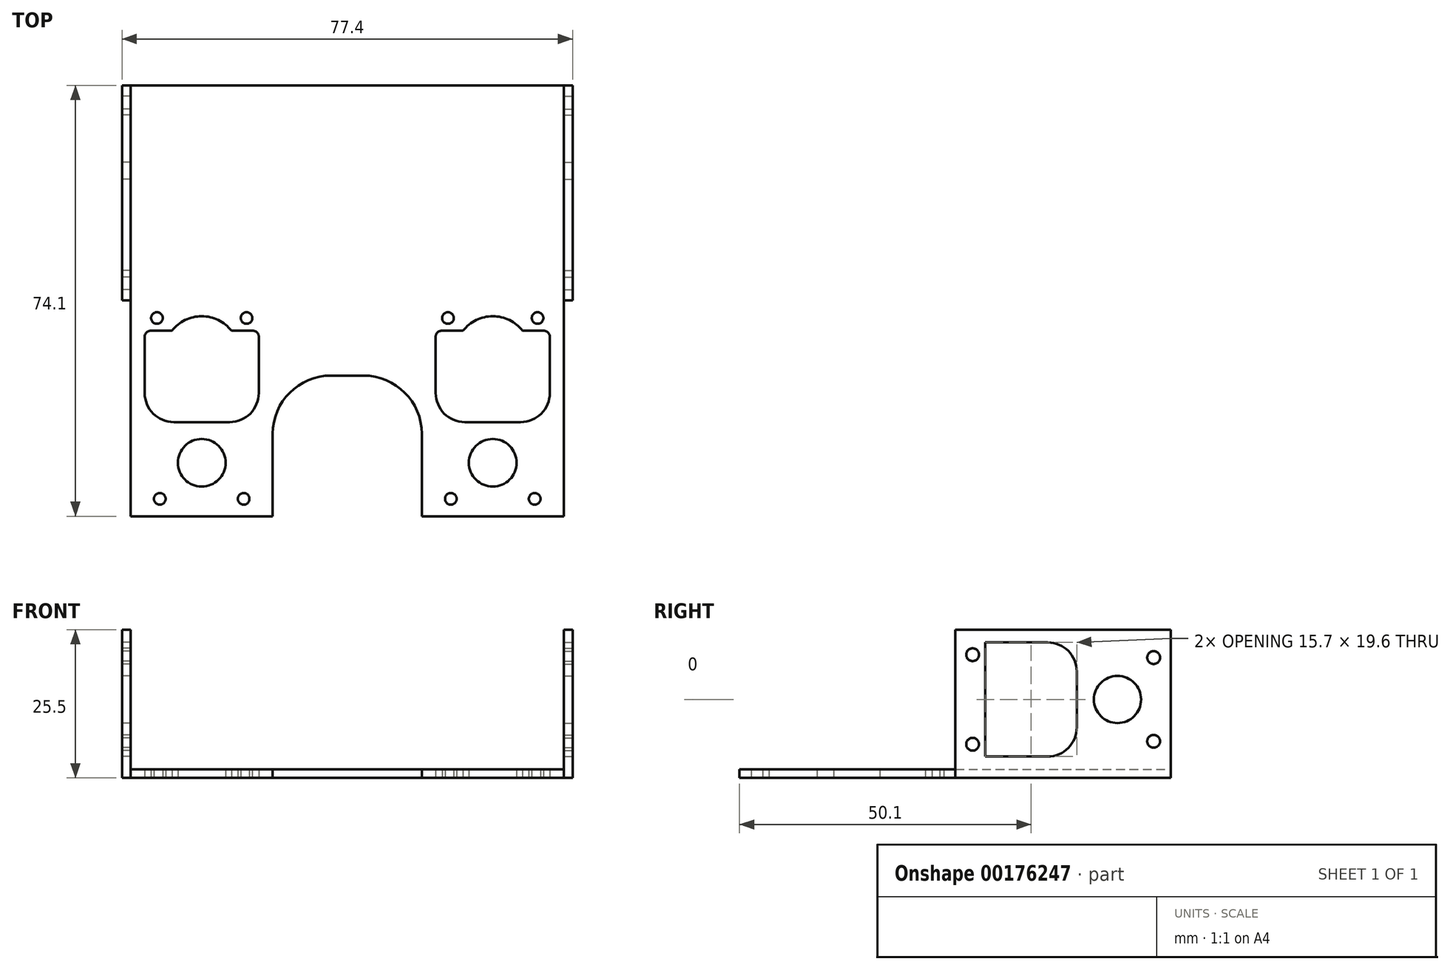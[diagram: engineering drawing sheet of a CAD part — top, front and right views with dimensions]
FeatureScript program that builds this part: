
annotation { "Feature Type Name" : "Feature", "Feature Type Description" : "" }
export const myFeature = defineFeature(function(context is Context, id is Id, definition is map)
    precondition{}
    {
        {
            var Q0;
            Q0=qCreatedBy(makeId("Top.planeOp"),FACE);
            var sketch = newSketch(context, id + "F0", { "sketchPlane" : qUnion([Q0])});
            skLineSegment(sketch, "E0.bottom", {"start": v(37.2, -19.55) * mm, "end": v(-37.2, -19.55) * mm});
            skLineSegment(sketch, "E0.top", {"start": v(37.2, 19.55) * mm, "end": v(-37.2, 19.55) * mm});
            skLineSegment(sketch, "E0.left", {"start": v(37.2, -19.55) * mm, "end": v(37.2, 19.55) * mm});
            skLineSegment(sketch, "E0.right", {"start": v(-37.2, -19.55) * mm, "end": v(-37.2, 19.55) * mm});
            skPoint(sketch, "E0.middle", {"position": v(0, 0) * mm});
            skCircle(sketch, "E1", {"center": v(25, 8.35) * mm, "radius": 4.1 * mm, "construction": true});
            skCircle(sketch, "E2", {"center": v(32.2, 14.55) * mm, "radius": 1 * mm, "construction": true});
            skLineSegment(sketch, "E3.bottom", {"start": v(33.8, -14.35) * mm, "end": v(30.12, -14.35) * mm, "construction": true});
            skLineSegment(sketch, "E3.top", {"start": v(29.8, 1.35) * mm, "end": v(20.2, 1.35) * mm, "construction": true});
            skLineSegment(sketch, "E3.left", {"start": v(34.8, -13.35) * mm, "end": v(34.8, -3.65) * mm, "construction": true});
            skLineSegment(sketch, "E3.right", {"start": v(15.2, -13.35) * mm, "end": v(15.2, -3.65) * mm, "construction": true});
            skPoint(sketch, "E3.middle", {"position": v(25, -6.5) * mm});
            skCircle(sketch, "E4", {"center": v(32.2, -16.55) * mm, "radius": 1 * mm});
            skPoint(sketch, "E5.visualSharp", {"position": v(15.2, 1.35) * mm});
            skArc(sketch, "E5.filletArc", {"start": v(20.2, 1.35) * mm, "mid": v(16.66, -0.11) * mm, "end": v(15.2, -3.65) * mm, "construction": true});
            skPoint(sketch, "E6.visualSharp", {"position": v(34.8, 1.35) * mm});
            skArc(sketch, "E6.filletArc", {"start": v(34.8, -3.65) * mm, "mid": v(33.34, -0.11) * mm, "end": v(29.8, 1.35) * mm, "construction": true});
            skPoint(sketch, "E7.visualSharp", {"position": v(15.2, -14.35) * mm});
            skArc(sketch, "E7.filletArc", {"start": v(15.2, -13.35) * mm, "mid": v(15.5, -14.06) * mm, "end": v(16.2, -14.35) * mm, "construction": true});
            skPoint(sketch, "E8.visualSharp", {"position": v(34.8, -14.35) * mm});
            skArc(sketch, "E8.filletArc", {"start": v(33.8, -14.35) * mm, "mid": v(34.5, -14.06) * mm, "end": v(34.8, -13.35) * mm, "construction": true});
            skArc(sketch, "E9", {"start": v(19.88, -14.35) * mm, "mid": v(25, -16.85) * mm, "end": v(30.12, -14.35) * mm, "construction": true});
            skLineSegment(sketch, "E10.trimOffspring", {"start": v(19.88, -14.35) * mm, "end": v(16.2, -14.35) * mm, "construction": true});
            skLineSegment(sketch, "E11", {"start": v(25, 19.55) * mm, "end": v(25, -19.55) * mm, "construction": true});
            skCircle(sketch, "E12.MirrorC", {"center": v(17.8, 14.55) * mm, "radius": 1 * mm, "construction": true});
            skCircle(sketch, "E13.MirrorC", {"center": v(17.8, -16.55) * mm, "radius": 1 * mm});
            skLineSegment(sketch, "E14", {"start": v(32.2, 14.55) * mm, "end": v(32.2, -16.55) * mm, "construction": true});
            skLineSegment(sketch, "E15", {"start": v(32.2, -1) * mm, "end": v(0, -1) * mm, "construction": true});
            skArc(sketch, "E16.MirrorCS", {"start": v(15.2, 11.35) * mm, "mid": v(15.5, 12.06) * mm, "end": v(16.2, 12.35) * mm});
            skArc(sketch, "E17.MirrorCS", {"start": v(33.8, 12.35) * mm, "mid": v(34.5, 12.06) * mm, "end": v(34.8, 11.35) * mm});
            skLineSegment(sketch, "E18.MirrorCS", {"start": v(15.2, 11.35) * mm, "end": v(15.2, 1.65) * mm});
            skLineSegment(sketch, "E19.MirrorCS", {"start": v(34.8, 11.35) * mm, "end": v(34.8, 1.65) * mm});
            skPoint(sketch, "E20.MirrorP", {"position": v(34.8, -3.35) * mm});
            skArc(sketch, "E21.MirrorCS", {"start": v(19.88, 12.35) * mm, "mid": v(25, 14.85) * mm, "end": v(30.12, 12.35) * mm});
            skPoint(sketch, "E22.MirrorP", {"position": v(15.2, -3.35) * mm});
            skPoint(sketch, "E23.MirrorP", {"position": v(25, 4.5) * mm});
            skCircle(sketch, "E24.MirrorC", {"center": v(25, -10.35) * mm, "radius": 4.1 * mm});
            skArc(sketch, "E25.MirrorCS", {"start": v(20.2, -3.35) * mm, "mid": v(16.66, -1.89) * mm, "end": v(15.2, 1.65) * mm});
            skLineSegment(sketch, "E26.MirrorCS", {"start": v(19.88, 12.35) * mm, "end": v(16.2, 12.35) * mm});
            skArc(sketch, "E27.MirrorCS", {"start": v(34.8, 1.65) * mm, "mid": v(33.34, -1.89) * mm, "end": v(29.8, -3.35) * mm});
            skPoint(sketch, "E28.MirrorP", {"position": v(34.8, 12.35) * mm});
            skLineSegment(sketch, "E29.MirrorCS", {"start": v(29.8, -3.35) * mm, "end": v(20.2, -3.35) * mm});
            skLineSegment(sketch, "E30.MirrorCS", {"start": v(33.8, 12.35) * mm, "end": v(30.12, 12.35) * mm});
            skPoint(sketch, "E31.MirrorP", {"position": v(15.2, 12.35) * mm});
            skArc(sketch, "E32.MirrorCS", {"start": v(-15.2, -13.35) * mm, "mid": v(-15.5, -14.06) * mm, "end": v(-16.2, -14.35) * mm, "construction": true});
            skArc(sketch, "E33.MirrorCS", {"start": v(-33.8, -14.35) * mm, "mid": v(-34.5, -14.06) * mm, "end": v(-34.8, -13.35) * mm, "construction": true});
            skArc(sketch, "E34.MirrorCS", {"start": v(-33.8, 12.35) * mm, "mid": v(-34.5, 12.06) * mm, "end": v(-34.8, 11.35) * mm});
            skArc(sketch, "E35.MirrorCS", {"start": v(-15.2, 11.35) * mm, "mid": v(-15.5, 12.06) * mm, "end": v(-16.2, 12.35) * mm});
            skPoint(sketch, "E36.MirrorP", {"position": v(-34.8, -14.35) * mm});
            skCircle(sketch, "E37.MirrorC", {"center": v(-25, 8.35) * mm, "radius": 4.1 * mm, "construction": true});
            skLineSegment(sketch, "E38.MirrorCS", {"start": v(-15.2, 11.35) * mm, "end": v(-15.2, 1.65) * mm});
            skArc(sketch, "E39.MirrorCS", {"start": v(-19.88, -14.35) * mm, "mid": v(-25, -16.85) * mm, "end": v(-30.12, -14.35) * mm, "construction": true});
            skCircle(sketch, "E40.MirrorC", {"center": v(-32.2, -16.55) * mm, "radius": 1 * mm});
            skLineSegment(sketch, "E41.MirrorCS", {"start": v(-33.8, -14.35) * mm, "end": v(-30.12, -14.35) * mm, "construction": true});
            skLineSegment(sketch, "E42.MirrorCS", {"start": v(-34.8, -13.35) * mm, "end": v(-34.8, -3.65) * mm, "construction": true});
            skCircle(sketch, "E43.MirrorC", {"center": v(-17.8, -16.55) * mm, "radius": 1 * mm});
            skPoint(sketch, "E44.MirrorP", {"position": v(-25, -6.5) * mm});
            skLineSegment(sketch, "E45.MirrorCS", {"start": v(-15.2, -13.35) * mm, "end": v(-15.2, -3.65) * mm, "construction": true});
            skPoint(sketch, "E46.MirrorP", {"position": v(-34.8, 12.35) * mm});
            skLineSegment(sketch, "E47.MirrorCS", {"start": v(-32.2, 14.55) * mm, "end": v(-32.2, -16.55) * mm, "construction": true});
            skLineSegment(sketch, "E48.MirrorCS", {"start": v(-34.8, 11.35) * mm, "end": v(-34.8, 1.65) * mm});
            skLineSegment(sketch, "E49.MirrorCS", {"start": v(-33.8, 12.35) * mm, "end": v(-30.12, 12.35) * mm});
            skArc(sketch, "E50.MirrorCS", {"start": v(-20.2, -3.35) * mm, "mid": v(-16.66, -1.89) * mm, "end": v(-15.2, 1.65) * mm});
            skArc(sketch, "E51.MirrorCS", {"start": v(-19.88, 12.35) * mm, "mid": v(-25, 14.85) * mm, "end": v(-30.12, 12.35) * mm});
            skLineSegment(sketch, "E52.MirrorCS", {"start": v(-19.88, 12.35) * mm, "end": v(-16.2, 12.35) * mm});
            skArc(sketch, "E53.MirrorCS", {"start": v(-34.8, -3.65) * mm, "mid": v(-33.34, -0.11) * mm, "end": v(-29.8, 1.35) * mm, "construction": true});
            skPoint(sketch, "E54.MirrorP", {"position": v(-15.2, 1.35) * mm});
            skCircle(sketch, "E55.MirrorC", {"center": v(-32.2, 14.55) * mm, "radius": 1 * mm, "construction": true});
            skPoint(sketch, "E56.MirrorP", {"position": v(-34.8, 1.35) * mm});
            skPoint(sketch, "E57.MirrorP", {"position": v(-15.2, -3.35) * mm});
            skLineSegment(sketch, "E58.MirrorCS", {"start": v(-29.8, 1.35) * mm, "end": v(-20.2, 1.35) * mm, "construction": true});
            skLineSegment(sketch, "E59.MirrorCS", {"start": v(-29.8, -3.35) * mm, "end": v(-20.2, -3.35) * mm});
            skPoint(sketch, "E60.MirrorP", {"position": v(-34.8, -3.35) * mm});
            skArc(sketch, "E61.MirrorCS", {"start": v(-20.2, 1.35) * mm, "mid": v(-16.66, -0.11) * mm, "end": v(-15.2, -3.65) * mm, "construction": true});
            skCircle(sketch, "E62.MirrorC", {"center": v(-25, -10.35) * mm, "radius": 4.1 * mm});
            skPoint(sketch, "E63.MirrorP", {"position": v(-15.2, -14.35) * mm});
            skPoint(sketch, "E64.MirrorP", {"position": v(-15.2, 12.35) * mm});
            skPoint(sketch, "E65.MirrorP", {"position": v(-25, 4.5) * mm});
            skArc(sketch, "E66.MirrorCS", {"start": v(-34.8, 1.65) * mm, "mid": v(-33.34, -1.89) * mm, "end": v(-29.8, -3.35) * mm});
            skCircle(sketch, "E67.MirrorC", {"center": v(-17.8, 14.55) * mm, "radius": 1 * mm, "construction": true});
            skLineSegment(sketch, "E68.MirrorCS", {"start": v(-19.88, -14.35) * mm, "end": v(-16.2, -14.35) * mm, "construction": true});
            skCircle(sketch, "E69", {"center": v(32.7, 14.55) * mm, "radius": 1 * mm, "construction": true});
            skCircle(sketch, "E70.MirrorC", {"center": v(17.3, 14.55) * mm, "radius": 1 * mm, "construction": true});
            skCircle(sketch, "E71.MirrorC", {"center": v(-32.7, 14.55) * mm, "radius": 1 * mm});
            skCircle(sketch, "E72.MirrorC", {"center": v(-17.3, 14.55) * mm, "radius": 1 * mm});
            skCircle(sketch, "E73", {"center": v(32.7, 14.55) * mm, "radius": 1 * mm});
            skCircle(sketch, "E74.MirrorC", {"center": v(17.3, 14.55) * mm, "radius": 1 * mm});
            skSolve(sketch);
        }
        {
            var Q0;
            Q0=qSketchRegion(id+"F0",true);
            extrude(context, id + "F1", {"entities" : qUnion([Q0]), "depth" : 1.5 * mm});
        }
        {
            var Q0;
            Q0=makeQuery(id+"F1.opExtrude","CAP_FACE",FACE,{"disambiguationData":[OSD([sQuery(id+"F0.wireOp",EDGE,"E0.bottom"),sQuery(id+"F0.wireOp",EDGE,"E0.top"),sQuery(id+"F0.wireOp",EDGE,"E0.left"),sQuery(id+"F0.wireOp",EDGE,"E0.right"),sQuery(id+"F0.wireOp",EDGE,"E2"),sQuery(id+"F0.wireOp",EDGE,"E4"),sQuery(id+"F0.wireOp",EDGE,"E12.MirrorC"),sQuery(id+"F0.wireOp",EDGE,"E13.MirrorC"),sQuery(id+"F0.wireOp",EDGE,"E16.MirrorCS"),sQuery(id+"F0.wireOp",EDGE,"E17.MirrorCS"),sQuery(id+"F0.wireOp",EDGE,"E18.MirrorCS"),sQuery(id+"F0.wireOp",EDGE,"E19.MirrorCS"),sQuery(id+"F0.wireOp",EDGE,"E21.MirrorCS"),sQuery(id+"F0.wireOp",EDGE,"E24.MirrorC"),sQuery(id+"F0.wireOp",EDGE,"E25.MirrorCS"),sQuery(id+"F0.wireOp",EDGE,"E26.MirrorCS"),sQuery(id+"F0.wireOp",EDGE,"E27.MirrorCS"),sQuery(id+"F0.wireOp",EDGE,"E29.MirrorCS"),sQuery(id+"F0.wireOp",EDGE,"E30.MirrorCS"),sQuery(id+"F0.wireOp",EDGE,"E34.MirrorCS"),sQuery(id+"F0.wireOp",EDGE,"E35.MirrorCS"),sQuery(id+"F0.wireOp",EDGE,"E38.MirrorCS"),sQuery(id+"F0.wireOp",EDGE,"E40.MirrorC"),sQuery(id+"F0.wireOp",EDGE,"E43.MirrorC"),sQuery(id+"F0.wireOp",EDGE,"E48.MirrorCS"),sQuery(id+"F0.wireOp",EDGE,"E49.MirrorCS"),sQuery(id+"F0.wireOp",EDGE,"E50.MirrorCS"),sQuery(id+"F0.wireOp",EDGE,"E51.MirrorCS"),sQuery(id+"F0.wireOp",EDGE,"E52.MirrorCS"),sQuery(id+"F0.wireOp",EDGE,"E55.MirrorC"),sQuery(id+"F0.wireOp",EDGE,"E59.MirrorCS"),sQuery(id+"F0.wireOp",EDGE,"E62.MirrorC"),sQuery(id+"F0.wireOp",EDGE,"E66.MirrorCS"),sQuery(id+"F0.wireOp",EDGE,"E67.MirrorC")])],"isStart":false});
            var sketch = newSketch(context, id + "F2", { "sketchPlane" : qUnion([Q0])});
            skLineSegment(sketch, "E75.bottom", {"start": v(-37.2, 19.55) * mm, "end": v(37.2, 19.55) * mm});
            skLineSegment(sketch, "E75.top", {"start": v(-37.2, 54.55) * mm, "end": v(37.2, 54.55) * mm});
            skLineSegment(sketch, "E75.left", {"start": v(-37.2, 19.55) * mm, "end": v(-37.2, 54.55) * mm});
            skLineSegment(sketch, "E75.right", {"start": v(37.2, 19.55) * mm, "end": v(37.2, 54.55) * mm});
            skPoint(sketch, "E76", {"position": v(-25, -10.35) * mm});
            skSolve(sketch);
        }
        {
            var Q0;
            Q0=qSketchRegion(id+"F2",true);
            extrude(context, id + "F3", {"entities" : qUnion([Q0]), "operationType" : NewBodyOperationType.ADD, "oppositeDirection" : true, "depth" : 1.5 * mm});
        }
        {
            var Q0;
            Q0=makeQuery(id+"F3.boolean.opBoolean","MERGE",FACE,{"derivedFrom":[makeQuery(id+"F1.opExtrude","CAP_FACE",FACE,{"disambiguationData":[OSD([sQuery(id+"F0.wireOp",EDGE,"E0.bottom"),sQuery(id+"F0.wireOp",EDGE,"E0.top"),sQuery(id+"F0.wireOp",EDGE,"E0.left"),sQuery(id+"F0.wireOp",EDGE,"E0.right"),sQuery(id+"F0.wireOp",EDGE,"E2"),sQuery(id+"F0.wireOp",EDGE,"E4"),sQuery(id+"F0.wireOp",EDGE,"E12.MirrorC"),sQuery(id+"F0.wireOp",EDGE,"E13.MirrorC"),sQuery(id+"F0.wireOp",EDGE,"E16.MirrorCS"),sQuery(id+"F0.wireOp",EDGE,"E17.MirrorCS"),sQuery(id+"F0.wireOp",EDGE,"E18.MirrorCS"),sQuery(id+"F0.wireOp",EDGE,"E19.MirrorCS"),sQuery(id+"F0.wireOp",EDGE,"E21.MirrorCS"),sQuery(id+"F0.wireOp",EDGE,"E24.MirrorC"),sQuery(id+"F0.wireOp",EDGE,"E25.MirrorCS"),sQuery(id+"F0.wireOp",EDGE,"E26.MirrorCS"),sQuery(id+"F0.wireOp",EDGE,"E27.MirrorCS"),sQuery(id+"F0.wireOp",EDGE,"E29.MirrorCS"),sQuery(id+"F0.wireOp",EDGE,"E30.MirrorCS"),sQuery(id+"F0.wireOp",EDGE,"E34.MirrorCS"),sQuery(id+"F0.wireOp",EDGE,"E35.MirrorCS"),sQuery(id+"F0.wireOp",EDGE,"E38.MirrorCS"),sQuery(id+"F0.wireOp",EDGE,"E40.MirrorC"),sQuery(id+"F0.wireOp",EDGE,"E43.MirrorC"),sQuery(id+"F0.wireOp",EDGE,"E48.MirrorCS"),sQuery(id+"F0.wireOp",EDGE,"E49.MirrorCS"),sQuery(id+"F0.wireOp",EDGE,"E50.MirrorCS"),sQuery(id+"F0.wireOp",EDGE,"E51.MirrorCS"),sQuery(id+"F0.wireOp",EDGE,"E52.MirrorCS"),sQuery(id+"F0.wireOp",EDGE,"E55.MirrorC"),sQuery(id+"F0.wireOp",EDGE,"E59.MirrorCS"),sQuery(id+"F0.wireOp",EDGE,"E62.MirrorC"),sQuery(id+"F0.wireOp",EDGE,"E66.MirrorCS"),sQuery(id+"F0.wireOp",EDGE,"E67.MirrorC")])],"isStart":false}),makeQuery(id+"F3.opExtrude","CAP_FACE",FACE,{"disambiguationData":[OSD([sQuery(id+"F2.wireOp",EDGE,"E75.bottom"),sQuery(id+"F2.wireOp",EDGE,"E75.top"),sQuery(id+"F2.wireOp",EDGE,"E75.left"),sQuery(id+"F2.wireOp",EDGE,"E75.right")])],"isStart":true})]});
            var sketch = newSketch(context, id + "F4", { "sketchPlane" : qUnion([Q0])});
            skLineSegment(sketch, "E77.bottom", {"start": v(-12.8, -19.55) * mm, "end": v(12.8, -19.55) * mm});
            skLineSegment(sketch, "E77.top", {"start": v(-12.8, 4.65) * mm, "end": v(12.8, 4.65) * mm});
            skLineSegment(sketch, "E77.left", {"start": v(-12.8, -19.55) * mm, "end": v(-12.8, 4.65) * mm});
            skLineSegment(sketch, "E77.right", {"start": v(12.8, -19.55) * mm, "end": v(12.8, 4.65) * mm});
            skPoint(sketch, "E78", {"position": v(0, -19.55) * mm});
            skPoint(sketch, "E79", {"position": v(-25, -10.35) * mm});
            skPoint(sketch, "E80", {"position": v(-32.2, -16.55) * mm});
            skPoint(sketch, "E81", {"position": v(-17.8, -16.55) * mm});
            skSolve(sketch);
        }
        {
            var Q0;
            Q0=qSketchRegion(id+"F4",true);
            extrude(context, id + "F5", {"entities" : qUnion([Q0]), "operationType" : NewBodyOperationType.REMOVE, "endBound" : BoundingType.UP_TO_NEXT, "oppositeDirection" : true, "depth" : 25 * mm});
        }
        {
            var Q0;
            Q0=makeQuery(id+"F5.boolean.opBoolean","COPY",EDGE,{"derivedFrom":makeQuery(id+"F5.opExtrude","SWEPT_EDGE",EDGE,{"disambiguationData":[OSD([sQuery(id+"F4.wireOp",EDGE,"E77.top"),sQuery(id+"F4.wireOp",EDGE,"E77.left")])]})});
            var Q1;
            Q1=makeQuery(id+"F5.boolean.opBoolean","COPY",EDGE,{"derivedFrom":makeQuery(id+"F5.opExtrude","SWEPT_EDGE",EDGE,{"disambiguationData":[OSD([sQuery(id+"F4.wireOp",EDGE,"E77.top"),sQuery(id+"F4.wireOp",EDGE,"E77.right")])]})});
            fillet(context, id + "F6", {"entities" : qUnion([Q0, Q1]), "radius" : 10 * mm, "tangentPropagation" : true, "allowEdgeOverflow" : false});
        }
        {
            var Q0;
            Q0=makeQuery(id+"F3.boolean.opBoolean","MERGE",FACE,{"derivedFrom":[makeQuery(id+"F1.opExtrude","CAP_FACE",FACE,{"disambiguationData":[OSD([sQuery(id+"F0.wireOp",EDGE,"E0.bottom"),sQuery(id+"F0.wireOp",EDGE,"E0.top"),sQuery(id+"F0.wireOp",EDGE,"E0.left"),sQuery(id+"F0.wireOp",EDGE,"E0.right"),sQuery(id+"F0.wireOp",EDGE,"E2"),sQuery(id+"F0.wireOp",EDGE,"E4"),sQuery(id+"F0.wireOp",EDGE,"E12.MirrorC"),sQuery(id+"F0.wireOp",EDGE,"E13.MirrorC"),sQuery(id+"F0.wireOp",EDGE,"E16.MirrorCS"),sQuery(id+"F0.wireOp",EDGE,"E17.MirrorCS"),sQuery(id+"F0.wireOp",EDGE,"E18.MirrorCS"),sQuery(id+"F0.wireOp",EDGE,"E19.MirrorCS"),sQuery(id+"F0.wireOp",EDGE,"E21.MirrorCS"),sQuery(id+"F0.wireOp",EDGE,"E24.MirrorC"),sQuery(id+"F0.wireOp",EDGE,"E25.MirrorCS"),sQuery(id+"F0.wireOp",EDGE,"E26.MirrorCS"),sQuery(id+"F0.wireOp",EDGE,"E27.MirrorCS"),sQuery(id+"F0.wireOp",EDGE,"E29.MirrorCS"),sQuery(id+"F0.wireOp",EDGE,"E30.MirrorCS"),sQuery(id+"F0.wireOp",EDGE,"E34.MirrorCS"),sQuery(id+"F0.wireOp",EDGE,"E35.MirrorCS"),sQuery(id+"F0.wireOp",EDGE,"E38.MirrorCS"),sQuery(id+"F0.wireOp",EDGE,"E40.MirrorC"),sQuery(id+"F0.wireOp",EDGE,"E43.MirrorC"),sQuery(id+"F0.wireOp",EDGE,"E48.MirrorCS"),sQuery(id+"F0.wireOp",EDGE,"E49.MirrorCS"),sQuery(id+"F0.wireOp",EDGE,"E50.MirrorCS"),sQuery(id+"F0.wireOp",EDGE,"E51.MirrorCS"),sQuery(id+"F0.wireOp",EDGE,"E52.MirrorCS"),sQuery(id+"F0.wireOp",EDGE,"E55.MirrorC"),sQuery(id+"F0.wireOp",EDGE,"E59.MirrorCS"),sQuery(id+"F0.wireOp",EDGE,"E62.MirrorC"),sQuery(id+"F0.wireOp",EDGE,"E66.MirrorCS"),sQuery(id+"F0.wireOp",EDGE,"E67.MirrorC")])],"isStart":false}),makeQuery(id+"F3.opExtrude","CAP_FACE",FACE,{"disambiguationData":[OSD([sQuery(id+"F2.wireOp",EDGE,"E75.bottom"),sQuery(id+"F2.wireOp",EDGE,"E75.top"),sQuery(id+"F2.wireOp",EDGE,"E75.left"),sQuery(id+"F2.wireOp",EDGE,"E75.right")])],"isStart":true})]});
            var sketch = newSketch(context, id + "F7", { "sketchPlane" : qUnion([Q0])});
            skLineSegment(sketch, "E82.bottom", {"start": v(37.2, 54.55) * mm, "end": v(38.7, 54.55) * mm});
            skLineSegment(sketch, "E82.top", {"start": v(37.2, 17.55) * mm, "end": v(38.7, 17.55) * mm});
            skLineSegment(sketch, "E82.left", {"start": v(37.2, 54.55) * mm, "end": v(37.2, 17.55) * mm});
            skLineSegment(sketch, "E82.right", {"start": v(38.7, 54.55) * mm, "end": v(38.7, 17.55) * mm});
            skSolve(sketch);
        }
        {
            var Q0;
            Q0=qSketchRegion(id+"F7",true);
            extrude(context, id + "F8", {"entities" : qUnion([Q0]), "operationType" : NewBodyOperationType.ADD, "depth" : (20 + 4) * mm, "hasSecondDirection" : true, "secondDirectionOppositeDirection" : true, "secondDirectionDepth" : 1.5 * mm});
        }
        {
            var Q0;
            Q0=makeQuery(id+"F8.opExtrude","SWEPT_FACE",FACE,{"disambiguationData":[OSD([sQuery(id+"F7.wireOp",EDGE,"E82.right")])]});
            var sketch = newSketch(context, id + "F9", { "sketchPlane" : qUnion([Q0])});
            skLineSegment(sketch, "E83", {"start": v(54.55, 13.5) * mm, "end": v(17.55, 13.5) * mm, "construction": true});
            skLineSegment(sketch, "E84", {"start": v(36.05, 25.5) * mm, "end": v(36.05, 0) * mm, "construction": true});
            skCircle(sketch, "E85", {"center": v(51.6, 20.7) * mm, "radius": 1.1 * mm});
            skCircle(sketch, "E86", {"center": v(45.4, 13.5) * mm, "radius": 4.05 * mm});
            skLineSegment(sketch, "E87.bottom", {"start": v(33.4, 23.3) * mm, "end": v(22.7, 23.3) * mm});
            skLineSegment(sketch, "E87.top", {"start": v(33.4, 3.7) * mm, "end": v(22.7, 3.7) * mm});
            skLineSegment(sketch, "E87.left", {"start": v(38.4, 18.3) * mm, "end": v(38.4, 8.7) * mm});
            skLineSegment(sketch, "E87.right", {"start": v(22.7, 23.3) * mm, "end": v(22.7, 3.7) * mm});
            skPoint(sketch, "E87.middle", {"position": v(30.55, 13.5) * mm});
            skPoint(sketch, "E88.visualSharp", {"position": v(38.4, 23.3) * mm});
            skArc(sketch, "E88.filletArc", {"start": v(38.4, 18.3) * mm, "mid": v(36.94, 21.84) * mm, "end": v(33.4, 23.3) * mm});
            skPoint(sketch, "E89.visualSharp", {"position": v(38.4, 3.7) * mm});
            skArc(sketch, "E89.filletArc", {"start": v(33.4, 3.7) * mm, "mid": v(36.94, 5.16) * mm, "end": v(38.4, 8.7) * mm});
            skCircle(sketch, "E90.MirrorC", {"center": v(51.6, 6.3) * mm, "radius": 1.1 * mm});
            skCircle(sketch, "E91.MirrorC", {"center": v(20.5, 20.7) * mm, "radius": 1.1 * mm, "construction": true});
            skCircle(sketch, "E92.MirrorC", {"center": v(20.5, 6.3) * mm, "radius": 1.1 * mm, "construction": true});
            skCircle(sketch, "E93", {"center": v(20.5, 21.2) * mm, "radius": 1.1 * mm});
            skCircle(sketch, "E94.MirrorC", {"center": v(20.5, 5.8) * mm, "radius": 1.1 * mm});
            skSolve(sketch);
        }
        {
            var Q0;
            Q0=qSketchRegion(id+"F9",true);
            extrude(context, id + "F10", {"entities" : qUnion([Q0]), "operationType" : NewBodyOperationType.REMOVE, "endBound" : BoundingType.UP_TO_NEXT, "oppositeDirection" : true, "depth" : 25 * mm});
        }
        {
            var Q0;
            Q0=makeQuery(id+"F1.opExtrude","SWEPT_BODY",BODY,{"disambiguationData":[OSD([sQuery(id+"F0.wireOp",EDGE,"E0.bottom"),sQuery(id+"F0.wireOp",EDGE,"E0.top"),sQuery(id+"F0.wireOp",EDGE,"E0.left"),sQuery(id+"F0.wireOp",EDGE,"E0.right"),sQuery(id+"F0.wireOp",EDGE,"E2"),sQuery(id+"F0.wireOp",EDGE,"E4"),sQuery(id+"F0.wireOp",EDGE,"E12.MirrorC"),sQuery(id+"F0.wireOp",EDGE,"E13.MirrorC"),sQuery(id+"F0.wireOp",EDGE,"E16.MirrorCS"),sQuery(id+"F0.wireOp",EDGE,"E17.MirrorCS"),sQuery(id+"F0.wireOp",EDGE,"E18.MirrorCS"),sQuery(id+"F0.wireOp",EDGE,"E19.MirrorCS"),sQuery(id+"F0.wireOp",EDGE,"E21.MirrorCS"),sQuery(id+"F0.wireOp",EDGE,"E24.MirrorC"),sQuery(id+"F0.wireOp",EDGE,"E25.MirrorCS"),sQuery(id+"F0.wireOp",EDGE,"E26.MirrorCS"),sQuery(id+"F0.wireOp",EDGE,"E27.MirrorCS"),sQuery(id+"F0.wireOp",EDGE,"E29.MirrorCS"),sQuery(id+"F0.wireOp",EDGE,"E30.MirrorCS"),sQuery(id+"F0.wireOp",EDGE,"E34.MirrorCS"),sQuery(id+"F0.wireOp",EDGE,"E35.MirrorCS"),sQuery(id+"F0.wireOp",EDGE,"E38.MirrorCS"),sQuery(id+"F0.wireOp",EDGE,"E40.MirrorC"),sQuery(id+"F0.wireOp",EDGE,"E43.MirrorC"),sQuery(id+"F0.wireOp",EDGE,"E48.MirrorCS"),sQuery(id+"F0.wireOp",EDGE,"E49.MirrorCS"),sQuery(id+"F0.wireOp",EDGE,"E50.MirrorCS"),sQuery(id+"F0.wireOp",EDGE,"E51.MirrorCS"),sQuery(id+"F0.wireOp",EDGE,"E52.MirrorCS"),sQuery(id+"F0.wireOp",EDGE,"E55.MirrorC"),sQuery(id+"F0.wireOp",EDGE,"E59.MirrorCS"),sQuery(id+"F0.wireOp",EDGE,"E62.MirrorC"),sQuery(id+"F0.wireOp",EDGE,"E66.MirrorCS"),sQuery(id+"F0.wireOp",EDGE,"E67.MirrorC")])]});
            var Q1;
            Q1=qCreatedBy(makeId("Right.planeOp"),FACE);
            mirror(context, id + "F11", {"operationType" : NewBodyOperationType.ADD, "entities" : qUnion([Q0]), "mirrorPlane" : qUnion([Q1])});
        }
    });
